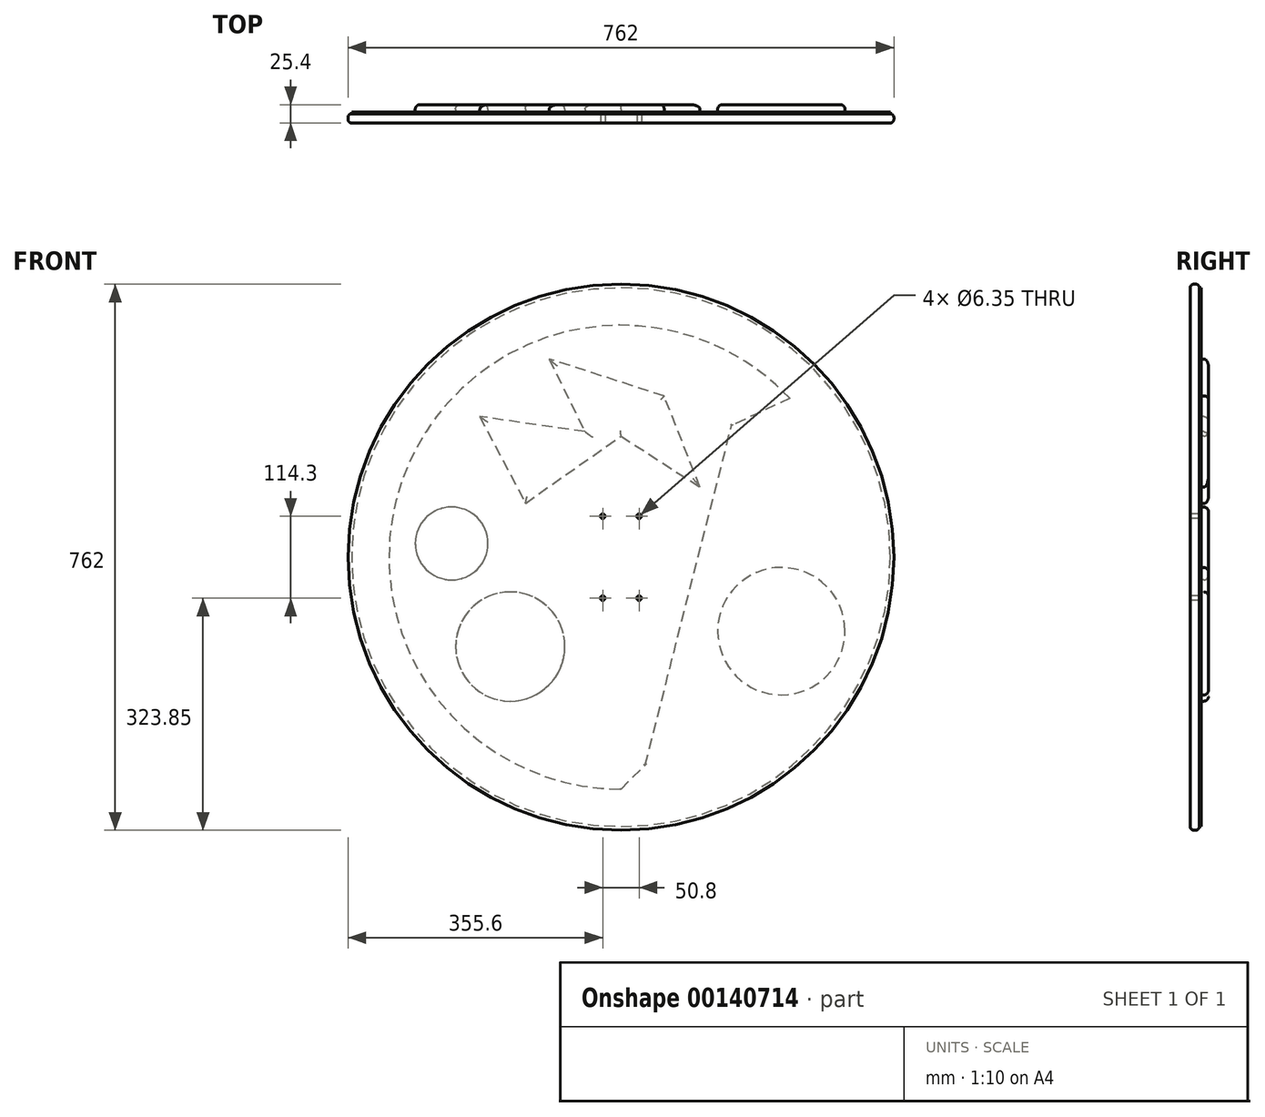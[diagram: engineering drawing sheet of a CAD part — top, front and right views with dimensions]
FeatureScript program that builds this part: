
annotation { "Feature Type Name" : "Feature", "Feature Type Description" : "" }
export const myFeature = defineFeature(function(context is Context, id is Id, definition is map)
    precondition{}
    {
        {
            var Q0;
            Q0=qCreatedBy(makeId("Front.planeOp"),FACE);
            var sketch = newSketch(context, id + "F0", { "sketchPlane" : qUnion([Q0])});
            skCircle(sketch, "E0", {"center": v(0, 0) * mm, "radius": 381 * mm});
            skSolve(sketch);
        }
        {
            var Q0;
            Q0 = qSketchRegion(id + "F0", true);
            extrude(context, id + "F1", {"entities" : qUnion([Q0]), "depth" : 12.7 * mm});
        }
        {
            var Q0;
            Q0=makeQuery(id+"F1.opExtrude","CAP_EDGE",EDGE,{"disambiguationData":[OSD([sQuery(id+"F0.wireOp",EDGE,"E0")])],"isStart":false});
            var Q1;
            Q1=makeQuery(id+"F1.opExtrude","CAP_EDGE",EDGE,{"disambiguationData":[OSD([sQuery(id+"F0.wireOp",EDGE,"E0")])],"isStart":true});
            fillet(context, id + "F2", {"entities" : qUnion([Q0, Q1]), "radius" : 5.08 * mm, "tangentPropagation" : true, "allowEdgeOverflow" : false});
        }
        {
            var Q0;
            Q0=makeQuery(id+"F1.opExtrude","CAP_FACE",FACE,{"disambiguationData":[OSD([sQuery(id+"F0.wireOp",EDGE,"E0")])],"isStart":false});
            var sketch = newSketch(context, id + "F3", { "sketchPlane" : qUnion([Q0])});
            skCircle(sketch, "E1", {"center": v(-25.4, 57.15) * mm, "radius": 3.17 * mm});
            skCircle(sketch, "E2", {"center": v(25.4, 57.15) * mm, "radius": 3.17 * mm});
            skCircle(sketch, "E3", {"center": v(-25.4, -57.15) * mm, "radius": 3.17 * mm});
            skCircle(sketch, "E4", {"center": v(25.4, -57.15) * mm, "radius": 3.17 * mm});
            skSolve(sketch);
        }
        {
            var Q0;
            Q0 = qSketchRegion(id + "F3", true);
            extrude(context, id + "F4", {"entities" : qUnion([Q0]), "operationType" : NewBodyOperationType.REMOVE, "oppositeDirection" : true, "depth" : 12.7 * mm});
        }
        {
            var Q0;
            Q0=makeQuery(id+"F1.opExtrude","CAP_FACE",FACE,{"disambiguationData":[OSD([sQuery(id+"F0.wireOp",EDGE,"E0")])],"isStart":true});
            var sketch = newSketch(context, id + "F5", { "sketchPlane" : qUnion([Q0])});
            skCircle(sketch, "E5", {"center": v(0, 0) * mm, "radius": 323.7 * mm});
            skLineSegment(sketch, "E6", {"start": v(13.83, 323.4) * mm, "end": v(323.7, 0) * mm});
            skLineSegment(sketch, "E7", {"start": v(323.7, 0) * mm, "end": v(0, -323.7) * mm});
            skLineSegment(sketch, "E8", {"start": v(0, -323.7) * mm, "end": v(-140.21, -183.48) * mm});
            skLineSegment(sketch, "E9", {"start": v(-282.39, -93.37) * mm, "end": v(-140.21, -183.48) * mm});
            skLineSegment(sketch, "E10", {"start": v(-282.39, -93.37) * mm, "end": v(-236.07, 221.47) * mm});
            skLineSegment(sketch, "E11", {"start": v(-236.07, 221.47) * mm, "end": v(-72.87, 146.5) * mm});
            skLineSegment(sketch, "E12", {"start": v(-72.87, 146.5) * mm, "end": v(13.83, 323.4) * mm});
            skLineSegment(sketch, "E13", {"start": v(142.58, 189.02) * mm, "end": v(-33.94, -289.76) * mm});
            skLineSegment(sketch, "E14", {"start": v(-33.94, -289.76) * mm, "end": v(-154.47, 183.99) * mm});
            skLineSegment(sketch, "E15", {"start": v(-154.47, 183.99) * mm, "end": v(88.34, 41.89) * mm});
            skSolve(sketch);
        }
        {
            var Q0;
            {var subQ0=sQuery(id+"F5.wireOp",EDGE,"E9");Q0=makeQuery(id+"F5.imprint","IMPRINT",FACE,{"disambiguationData":[TD([[makeQuery(id+"F5.imprint","IMPRINT",EDGE,{"derivedFrom":subQ0}),-1.0]])]});}
            var Q1;
            {var subQ3=sQuery(id+"F5.wireOp",EDGE,"E9");Q1=makeQuery(id+"F5.imprint","IMPRINT",FACE,{"disambiguationData":[TD([[makeQuery(id+"F5.imprint","IMPRINT",EDGE,{"derivedFrom":subQ3}),1.0]])]});}
            var Q2;
            {var subQ7=sQuery(id+"F0.wireOp",EDGE,"E0");Q2=makeQuery(id+"F5.imprint","IMPRINT",FACE,{"disambiguationData":[TD([[makeQuery(id+"F5.imprint","IMPRINT",EDGE,{"derivedFrom":makeQuery(id+"F2.opFillet","BLEND_EDGE",EDGE,{"blendedFrom":[makeQuery(id+"F1.opExtrude","CAP_EDGE",EDGE,{"disambiguationData":[OSD([subQ7])],"isStart":true}),makeQuery(id+"F1.opExtrude","CAP_FACE",FACE,{"disambiguationData":[OSD([subQ7])],"isStart":true})],"blendedInto":[makeQuery(id+"F1.opExtrude","CAP_FACE",FACE,{"disambiguationData":[OSD([subQ7])],"isStart":true})]})}),1.0]])]});}
            extrude(context, id + "F6", {"entities" : qUnion([Q0, Q1, Q2]), "operationType" : NewBodyOperationType.ADD, "depth" : 2.54 * mm});
        }
        {
            var Q0;
            Q0=makeQuery(id+"F6.opExtrude","CAP_EDGE",EDGE,{"disambiguationData":[OSD([sQuery(id+"F5.wireOp",EDGE,"E14")])],"isStart":false});
            var Q1;
            Q1=makeQuery(id+"F1.opExtrude","CAP_FACE",FACE,{"disambiguationData":[OSD([sQuery(id+"F0.wireOp",EDGE,"E0")])],"isStart":true});
            fillet(context, id + "F7", {"entities" : qUnion([Q0, Q1]), "radius" : 1.27 * mm, "tangentPropagation" : true, "allowEdgeOverflow" : false});
        }
        {
            var Q0;
            Q0=makeQuery(id+"F1.opExtrude","CAP_FACE",FACE,{"disambiguationData":[OSD([sQuery(id+"F0.wireOp",EDGE,"E0")])],"isStart":true});
            var sketch = newSketch(context, id + "F8", { "sketchPlane" : qUnion([Q0])});
            skCircle(sketch, "E16", {"center": v(-223.94, -103.24) * mm, "radius": 88.9 * mm});
            skCircle(sketch, "E17", {"center": v(236.3, 19.12) * mm, "radius": 50.8 * mm});
            skCircle(sketch, "E18", {"center": v(154.55, -124.7) * mm, "radius": 76.2 * mm});
            skLineSegment(sketch, "E19", {"start": v(-60.42, 225) * mm, "end": v(100.05, 276.47) * mm});
            skLineSegment(sketch, "E20", {"start": v(100.05, 276.47) * mm, "end": v(50.1, 175.04) * mm});
            skLineSegment(sketch, "E21", {"start": v(50.1, 175.04) * mm, "end": v(196.94, 196.24) * mm});
            skLineSegment(sketch, "E22", {"start": v(196.94, 196.24) * mm, "end": v(133.36, 75.13) * mm});
            skLineSegment(sketch, "E23", {"start": v(133.36, 75.13) * mm, "end": v(0, 168.99) * mm});
            skLineSegment(sketch, "E24", {"start": v(0, 168.99) * mm, "end": v(-110.37, 97.84) * mm});
            skLineSegment(sketch, "E25", {"start": v(-110.37, 97.84) * mm, "end": v(-60.42, 225) * mm});
            skSolve(sketch);
        }
        {
            var Q0;
            Q0 = qSketchRegion(id + "F8", true);
            extrude(context, id + "F9", {"entities" : qUnion([Q0]), "operationType" : NewBodyOperationType.ADD, "depth" : 12.7 * mm});
        }
        {
            var Q0;
            Q0=makeQuery(id+"F9.opExtrude","CAP_EDGE",EDGE,{"disambiguationData":[OSD([sQuery(id+"F8.wireOp",EDGE,"E23")])],"isStart":false});
            var Q1;
            Q1=makeQuery(id+"F9.opExtrude","CAP_EDGE",EDGE,{"disambiguationData":[OSD([sQuery(id+"F8.wireOp",EDGE,"E22")])],"isStart":false});
            var Q2;
            Q2=makeQuery(id+"F9.opExtrude","CAP_EDGE",EDGE,{"disambiguationData":[OSD([sQuery(id+"F8.wireOp",EDGE,"E24")])],"isStart":false});
            var Q3;
            Q3=makeQuery(id+"F9.opExtrude","CAP_EDGE",EDGE,{"disambiguationData":[OSD([sQuery(id+"F8.wireOp",EDGE,"E25")])],"isStart":false});
            var Q4;
            Q4=makeQuery(id+"F9.opExtrude","CAP_EDGE",EDGE,{"disambiguationData":[OSD([sQuery(id+"F8.wireOp",EDGE,"E22")])],"isStart":true});
            var Q5;
            Q5=makeQuery(id+"F9.opExtrude","CAP_EDGE",EDGE,{"disambiguationData":[OSD([sQuery(id+"F8.wireOp",EDGE,"E23")])],"isStart":true});
            var Q6;
            Q6=makeQuery(id+"F9.opExtrude","CAP_EDGE",EDGE,{"disambiguationData":[OSD([sQuery(id+"F8.wireOp",EDGE,"E24")])],"isStart":true});
            var Q7;
            Q7=makeQuery(id+"F9.opExtrude","CAP_EDGE",EDGE,{"disambiguationData":[OSD([sQuery(id+"F8.wireOp",EDGE,"E20")])],"isStart":false});
            var Q8;
            Q8=makeQuery(id+"F9.opExtrude","CAP_EDGE",EDGE,{"disambiguationData":[OSD([sQuery(id+"F8.wireOp",EDGE,"E21")])],"isStart":false});
            var Q9;
            Q9=makeQuery(id+"F9.opExtrude","CAP_EDGE",EDGE,{"disambiguationData":[OSD([sQuery(id+"F8.wireOp",EDGE,"E19")])],"isStart":false});
            var Q10;
            Q10=makeQuery(id+"F9.opExtrude","CAP_EDGE",EDGE,{"disambiguationData":[OSD([sQuery(id+"F8.wireOp",EDGE,"E20")])],"isStart":true});
            var Q11;
            Q11=makeQuery(id+"F9.opExtrude","CAP_EDGE",EDGE,{"disambiguationData":[OSD([sQuery(id+"F8.wireOp",EDGE,"E17")])],"isStart":true});
            var Q12;
            Q12=makeQuery(id+"F9.opExtrude","CAP_EDGE",EDGE,{"disambiguationData":[OSD([sQuery(id+"F8.wireOp",EDGE,"E17")])],"isStart":false});
            var Q13;
            Q13=makeQuery(id+"F9.opExtrude","CAP_EDGE",EDGE,{"disambiguationData":[OSD([sQuery(id+"F8.wireOp",EDGE,"E18")])],"isStart":false});
            var Q14;
            Q14=makeQuery(id+"F9.opExtrude","CAP_EDGE",EDGE,{"disambiguationData":[OSD([sQuery(id+"F8.wireOp",EDGE,"E18")])],"isStart":true});
            var Q15;
            Q15=makeQuery(id+"F9.opExtrude","CAP_EDGE",EDGE,{"disambiguationData":[OSD([sQuery(id+"F8.wireOp",EDGE,"E16")])],"isStart":false});
            fillet(context, id + "F10", {"entities" : qUnion([Q0, Q1, Q2, Q3, Q4, Q5, Q6, Q7, Q8, Q9, Q10, Q11, Q12, Q13, Q14, Q15]), "radius" : 6.35 * mm, "tangentPropagation" : true, "allowEdgeOverflow" : false});
        }
    });
